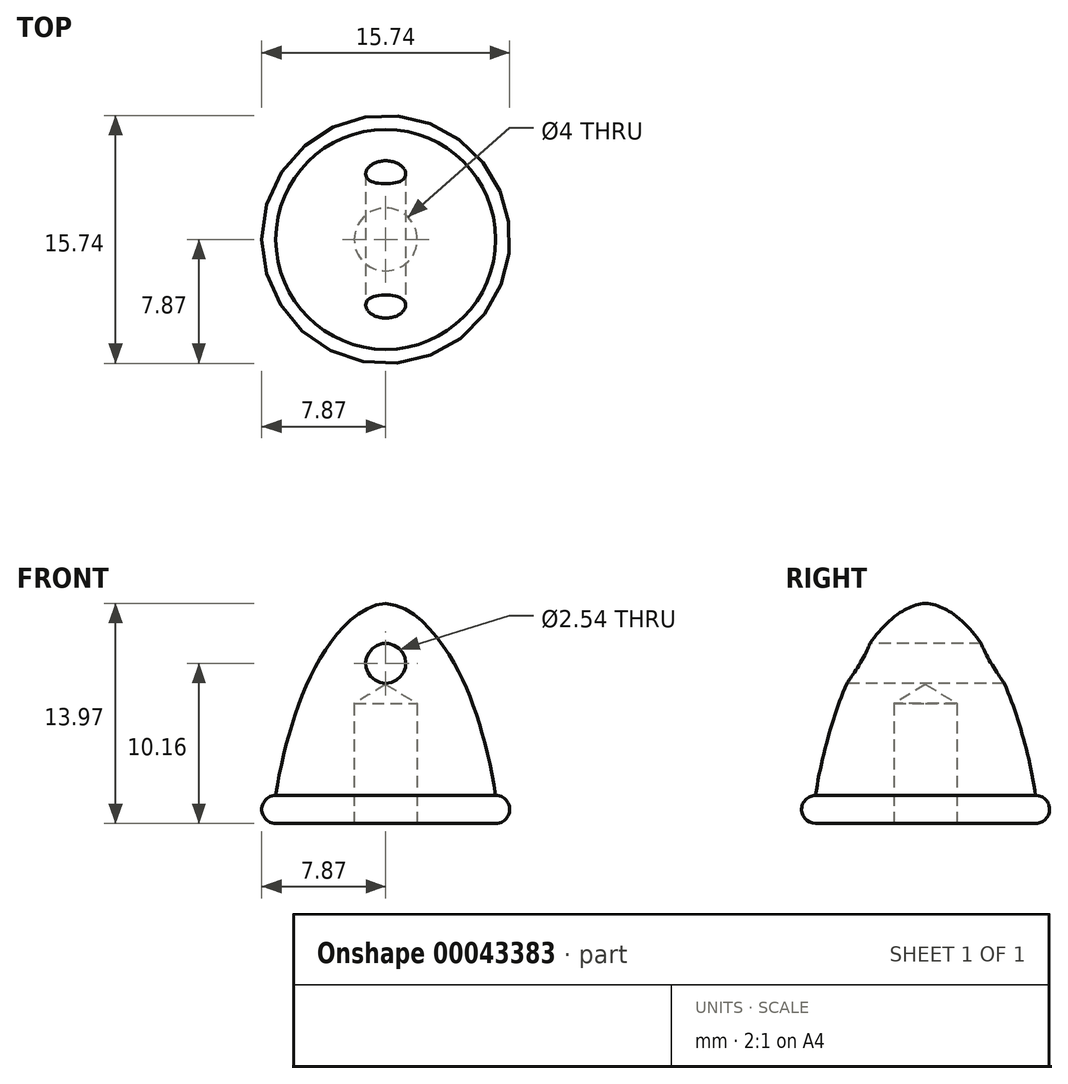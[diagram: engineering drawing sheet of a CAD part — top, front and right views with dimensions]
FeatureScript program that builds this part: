
annotation { "Feature Type Name" : "Feature", "Feature Type Description" : "" }
export const myFeature = defineFeature(function(context is Context, id is Id, definition is map)
    precondition{}
    {
        {
            var Q0;
            Q0=qCreatedBy(makeId("Front.planeOp"),FACE);
            var sketch = newSketch(context, id + "F0", { "sketchPlane" : qUnion([Q0])});
            skLineSegment(sketch, "E0", {"start": v(0, 0) * mm, "end": v(0, 22.8) * mm, "construction": true});
            skLineSegment(sketch, "E1", {"start": v(0, 0) * mm, "end": v(6.99, 0) * mm});
            skFitSpline(sketch, "E2", {"points": [v(0, 13.97) * mm, v(3.93, 10.85) * mm, v(5.75, 6.91) * mm, v(6.99, 1.78) * mm], "startDerivative": vector(14.92, -1.04) * mm, "endDerivative": vector(2.12, -15.08) * mm});
            skArc(sketch, "E3", {"start": v(6.99, 0) * mm, "mid": v(7.87, 0.89) * mm, "end": v(6.99, 1.78) * mm});
            skLineSegment(sketch, "E4", {"start": v(0, 13.97) * mm, "end": v(0, 0) * mm});
            skSolve(sketch);
        }
        {
            var Q0;
            Q0 = qSketchRegion(id + "F0", true);
            var Q1;
            Q1=sQuery(id+"F0.wireOp",EDGE,"E0");
            revolve(context, id + "F1", {"entities" : qUnion([Q0]), "axis" : qUnion([Q1]), "revolveType" : RevolveType.FULL});
        }
        {
            var Q0;
            Q0=qCreatedBy(makeId("Front.planeOp"),FACE);
            var sketch = newSketch(context, id + "F2", { "sketchPlane" : qUnion([Q0])});
            skCircle(sketch, "E5", {"center": v(0, 10.16) * mm, "radius": 1.27 * mm});
            skSolve(sketch);
        }
        {
            var Q0;
            Q0 = qSketchRegion(id + "F2", true);
            extrude(context, id + "F3", {"entities" : qUnion([Q0]), "operationType" : NewBodyOperationType.REMOVE, "endBound" : BoundingType.THROUGH_ALL, "oppositeDirection" : true, "depth" : 25.4 * mm, "hasSecondDirection" : true, "secondDirectionBound" : SecondDirectionBoundingType.THROUGH_ALL, "secondDirectionOppositeDirection" : false, "secondDirectionDepth" : 25.4 * mm});
        }
        {
            var Q0;
            Q0=makeQuery(id+"F1.opRevolve","SWEPT_FACE",FACE,{"disambiguationData":[OSD([sQuery(id+"F0.wireOp",EDGE,"E1")])]});
            var sketch = newSketch(context, id + "F4", { "sketchPlane" : qUnion([Q0])});
            skPoint(sketch, "E6", {"position": v(0, 0) * mm});
            skSolve(sketch);
        }
        {
            var Q0;
            Q0=sQuery(id+"F4.wireOp",VERTEX,"E6");
            var Q1;
            Q1=makeQuery(id+"F1.opRevolve","SWEPT_BODY",BODY,{"disambiguationData":[OSD([sQuery(id+"F0.wireOp",EDGE,"E1"),sQuery(id+"F0.wireOp",EDGE,"E2"),sQuery(id+"F0.wireOp",EDGE,"E3"),sQuery(id+"F0.wireOp",EDGE,"E4")])]});
            hole(context, id + "F5", {"style" : HoleStyle.SIMPLE, "holeDiameter" : 4 * mm, "endStyle" : HoleEndStyle.BLIND, "holeDepth" : 7.62 * mm, "locations" : qUnion([Q0]), "scope" : qUnion([Q1])});
        }
    });
